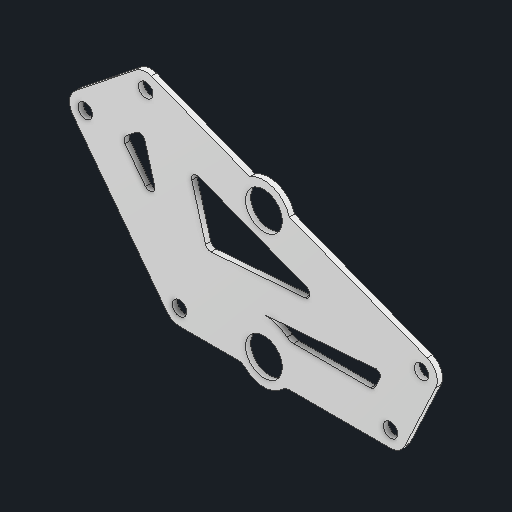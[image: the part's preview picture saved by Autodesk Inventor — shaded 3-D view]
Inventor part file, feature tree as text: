
AUTODESK INVENTOR PART (.ipt)
format: ipt  version: 2025 (Build 290162000, 162)  size: 184,320 bytes
history: native  units: in
note: dims shown in document units (in); Inventor stores cm internally (conversion verified against a paired STEP export)
features: other x3, extrude x1, sketch x1
ambient origin geometry x8: Origin, YZ Plane, XZ Plane, XY Plane, X Axis, Y Axis, Z Axis, Center Point
bodies: Solid1 (feature_tree)
feature tree (5):
  other  "Blocks"
  extrude  "Extrusion1"  Depth=0.375in
  sketch  "Sketch1"  dims[d0=0.375in d1=0.375in d2=0.375in d3=0.375in d4=0.375in d5=0.5in d7=0.375in d8=0.0625in d9=0.0625in d10=0.0625in d11=0.0in d13=0.4375in d14=0.5in d15=0.625in d16=0.125in d18=0.4375in d19=0.625in d20=0.5in d21=0.5in d22=0.5in d23=0.5in]
  other  "main"
  other  "main:1"
